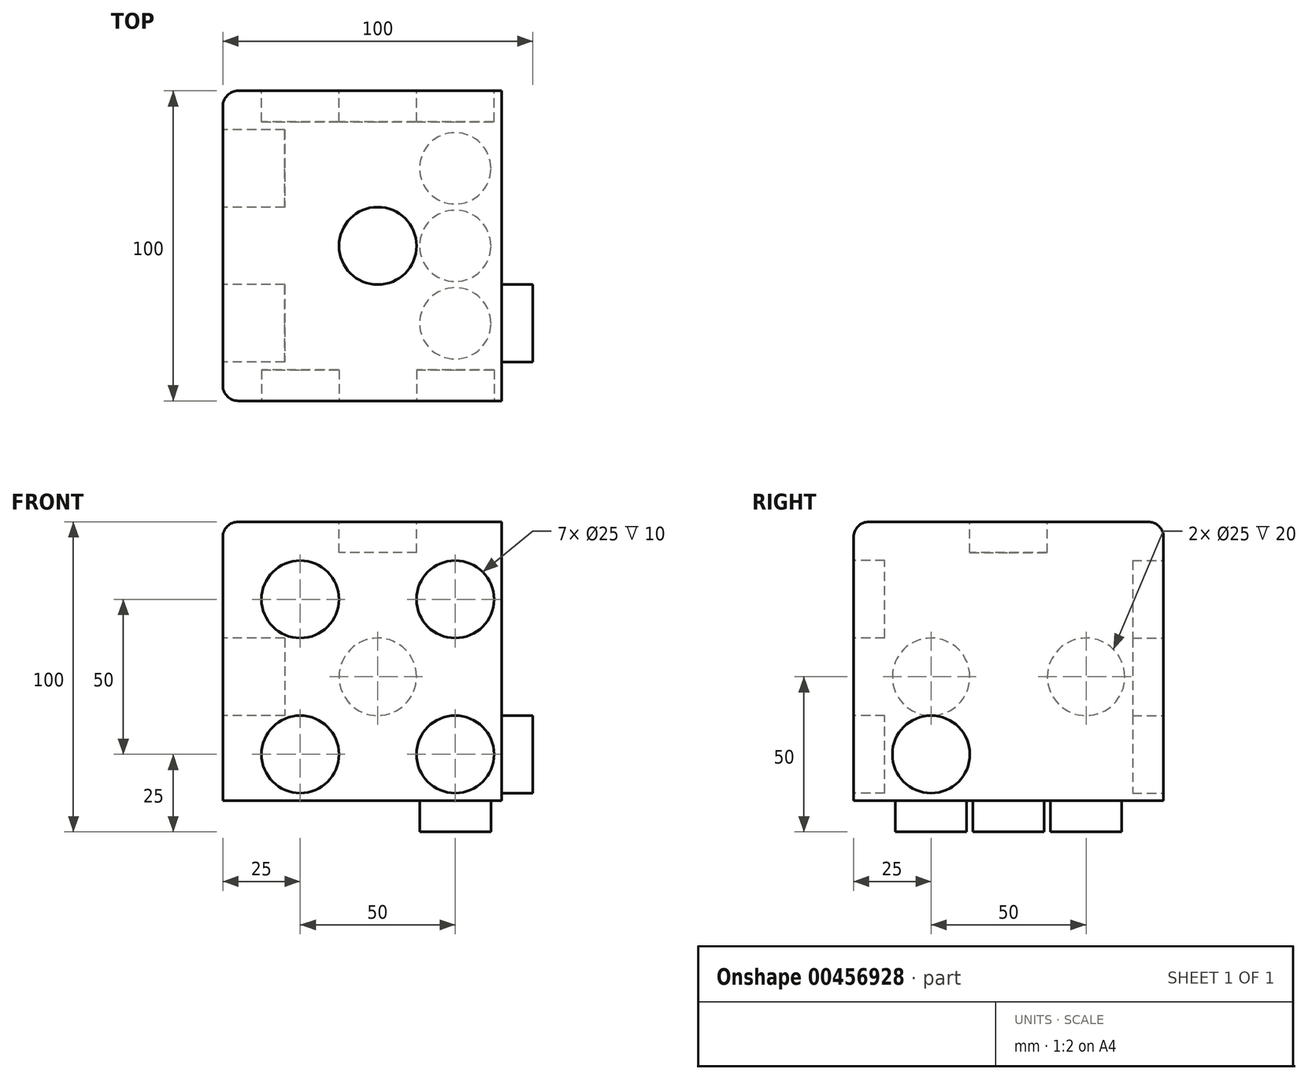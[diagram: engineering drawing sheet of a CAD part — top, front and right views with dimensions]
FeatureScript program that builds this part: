
annotation { "Feature Type Name" : "Feature", "Feature Type Description" : "" }
export const myFeature = defineFeature(function(context is Context, id is Id, definition is map)
    precondition{}
    {
        {
            var Q0;
            Q0=qCreatedBy(makeId("Top.planeOp"),FACE);
            var sketch = newSketch(context, id + "F0", { "sketchPlane" : qUnion([Q0])});
            skLineSegment(sketch, "E0.bottom", {"start": v(50, -50) * mm, "end": v(-50, -50) * mm});
            skLineSegment(sketch, "E0.top", {"start": v(50, 50) * mm, "end": v(-50, 50) * mm});
            skLineSegment(sketch, "E0.left", {"start": v(50, -50) * mm, "end": v(50, 50) * mm});
            skLineSegment(sketch, "E0.right", {"start": v(-50, -50) * mm, "end": v(-50, 50) * mm});
            skPoint(sketch, "E0.middle", {"position": v(0, 0) * mm});
            skLineSegment(sketch, "E1", {"start": v(-50, 50) * mm, "end": v(50, -50) * mm, "construction": true});
            skLineSegment(sketch, "E2", {"start": v(-50, -50) * mm, "end": v(50, 50) * mm, "construction": true});
            skLineSegment(sketch, "E3", {"start": v(-50, 0) * mm, "end": v(50, 0) * mm, "construction": true});
            skLineSegment(sketch, "E4", {"start": v(0, 50) * mm, "end": v(0, -50) * mm, "construction": true});
            skSolve(sketch);
        }
        {
            var Q0;
            Q0=makeQuery(id+"F0.imprint","IMPRINT",FACE,{"disambiguationData":[TD([[makeQuery(id+"F0.imprint","IMPRINT",EDGE,{"derivedFrom":sQuery(id+"F0.wireOp",EDGE,"E0.bottom")}),-1.0]])]});
            extrude(context, id + "F1", {"entities" : qUnion([Q0]), "depth" : 100 * mm});
        }
        {
            var Q0;
            Q0=makeQuery(id+"F1.opExtrude","CAP_FACE",FACE,{"disambiguationData":[OSD([sQuery(id+"F0.wireOp",EDGE,"E0.bottom"),sQuery(id+"F0.wireOp",EDGE,"E0.top"),sQuery(id+"F0.wireOp",EDGE,"E0.left"),sQuery(id+"F0.wireOp",EDGE,"E0.right")])],"isStart":false});
            var sketch = newSketch(context, id + "F2", { "sketchPlane" : qUnion([Q0])});
            skSolve(sketch);
        }
        {
            var Q0;
            Q0=makeQuery(id+"F2.imprint","IMPRINT",FACE,{"disambiguationData":[TD([[makeQuery(id+"F2.imprint","IMPRINT",EDGE,{"derivedFrom":makeQuery(id+"F1.opExtrude","CAP_EDGE",EDGE,{"disambiguationData":[OSD([sQuery(id+"F0.wireOp",EDGE,"E0.bottom")])],"isStart":false})}),-1.0]])]});
            var sketch = newSketch(context, id + "F3", { "sketchPlane" : qUnion([Q0])});
            skCircle(sketch, "E5", {"center": v(0, 0) * mm, "radius": 12.5 * mm});
            skSolve(sketch);
        }
        {
            var Q0;
            Q0 = qSketchRegion(id + "F3", true);
            extrude(context, id + "F4", {"entities" : qUnion([Q0]), "operationType" : NewBodyOperationType.REMOVE, "oppositeDirection" : true, "depth" : 10 * mm});
        }
        {
            var Q0;
            Q0=makeQuery(id+"F1.opExtrude","SWEPT_FACE",FACE,{"disambiguationData":[OSD([sQuery(id+"F0.wireOp",EDGE,"E0.right")])]});
            var sketch = newSketch(context, id + "F5", { "sketchPlane" : qUnion([Q0])});
            skLineSegment(sketch, "E6", {"start": v(0, 0) * mm, "end": v(0, 100) * mm, "construction": true});
            skLineSegment(sketch, "E7", {"start": v(50, 50) * mm, "end": v(-50, 50) * mm, "construction": true});
            skLineSegment(sketch, "E8", {"start": v(-50, 100) * mm, "end": v(50, 0) * mm, "construction": true});
            skLineSegment(sketch, "E9", {"start": v(50, 100) * mm, "end": v(-50, 0) * mm, "construction": true});
            skLineSegment(sketch, "E10", {"start": v(-50, 50) * mm, "end": v(0, 100) * mm, "construction": true});
            skLineSegment(sketch, "E11", {"start": v(-50, 50) * mm, "end": v(0, 0) * mm, "construction": true});
            skLineSegment(sketch, "E12", {"start": v(-25, 75) * mm, "end": v(-25, 25) * mm, "construction": true});
            skLineSegment(sketch, "E13", {"start": v(-25, 25) * mm, "end": v(25, 25) * mm, "construction": true});
            skLineSegment(sketch, "E14", {"start": v(25, 25) * mm, "end": v(25, 75) * mm, "construction": true});
            skLineSegment(sketch, "E15", {"start": v(25, 75) * mm, "end": v(-25, 75) * mm, "construction": true});
            skSolve(sketch);
        }
        {
            var Q0;
            {var subQ0=sQuery(id+"F0.wireOp",EDGE,"E0.right");Q0=makeQuery(id+"F5.imprint","IMPRINT",FACE,{"disambiguationData":[TD([[makeQuery(id+"F5.imprint","IMPRINT",EDGE,{"derivedFrom":makeQuery(id+"F1.opExtrude","CAP_EDGE",EDGE,{"disambiguationData":[OSD([subQ0])],"isStart":true})}),-1.0]])]});}
            var sketch = newSketch(context, id + "F6", { "sketchPlane" : qUnion([Q0])});
            skSolve(sketch);
        }
        {
            var Q0;
            {var subQ0=sQuery(id+"F0.wireOp",EDGE,"E0.right");Q0=makeQuery(id+"F5.imprint","IMPRINT",FACE,{"disambiguationData":[TD([[makeQuery(id+"F5.imprint","IMPRINT",EDGE,{"derivedFrom":makeQuery(id+"F1.opExtrude","CAP_EDGE",EDGE,{"disambiguationData":[OSD([subQ0])],"isStart":true})}),-1.0]])]});}
            var sketch = newSketch(context, id + "F7", { "sketchPlane" : qUnion([Q0])});
            skCircle(sketch, "E16", {"center": v(-25, 50) * mm, "radius": 12.5 * mm});
            skCircle(sketch, "E17", {"center": v(25, 50) * mm, "radius": 12.5 * mm});
            skSolve(sketch);
        }
        {
            var Q0;
            Q0 = qSketchRegion(id + "F7", true);
            extrude(context, id + "F8", {"entities" : qUnion([Q0]), "operationType" : NewBodyOperationType.REMOVE, "oppositeDirection" : true, "depth" : 20 * mm});
        }
        {
            var Q0;
            Q0=makeQuery(id+"F1.opExtrude","SWEPT_FACE",FACE,{"disambiguationData":[OSD([sQuery(id+"F0.wireOp",EDGE,"E0.top")])]});
            var sketch = newSketch(context, id + "F9", { "sketchPlane" : qUnion([Q0])});
            skLineSegment(sketch, "E18", {"start": v(50, 100) * mm, "end": v(-50, 0) * mm, "construction": true});
            skSolve(sketch);
        }
        {
            var Q0;
            {var subQ0=sQuery(id+"F0.wireOp",EDGE,"E0.top");Q0=makeQuery(id+"F9.imprint","IMPRINT",FACE,{"disambiguationData":[TD([[makeQuery(id+"F9.imprint","IMPRINT",EDGE,{"derivedFrom":makeQuery(id+"F1.opExtrude","CAP_EDGE",EDGE,{"disambiguationData":[OSD([subQ0])],"isStart":true})}),1.0]])]});}
            var sketch = newSketch(context, id + "F10", { "sketchPlane" : qUnion([Q0])});
            skCircle(sketch, "E19", {"center": v(0, 50) * mm, "radius": 12.5 * mm});
            skSolve(sketch);
        }
        {
            var Q0;
            Q0=makeQuery(id+"F10.imprint","IMPRINT",FACE,{"disambiguationData":[TD([[makeQuery(id+"F10.imprint","IMPRINT",EDGE,{"derivedFrom":sQuery(id+"F10.wireOp",EDGE,"E19")}),-1.0]])]});
            var sketch = newSketch(context, id + "F11", { "sketchPlane" : qUnion([Q0])});
            skLineSegment(sketch, "E20", {"start": v(-50, 0) * mm, "end": v(0, 50) * mm, "construction": true});
            skLineSegment(sketch, "E21", {"start": v(0, 50) * mm, "end": v(50, 100) * mm, "construction": true});
            skLineSegment(sketch, "E22", {"start": v(0, 50) * mm, "end": v(-50, 50) * mm, "construction": true});
            skLineSegment(sketch, "E23", {"start": v(-50, 50) * mm, "end": v(0, 0) * mm, "construction": true});
            skCircle(sketch, "E24", {"center": v(-25, 25) * mm, "radius": 12.5 * mm});
            skLineSegment(sketch, "E25", {"start": v(0, 50) * mm, "end": v(50, 50) * mm, "construction": true});
            skLineSegment(sketch, "E26", {"start": v(50, 50) * mm, "end": v(0, 100) * mm, "construction": true});
            skCircle(sketch, "E27", {"center": v(25, 75) * mm, "radius": 12.5 * mm});
            skSolve(sketch);
        }
        {
            var Q0;
            Q0=makeQuery(id+"F10.imprint","IMPRINT",FACE,{"disambiguationData":[TD([[makeQuery(id+"F10.imprint","IMPRINT",EDGE,{"derivedFrom":sQuery(id+"F10.wireOp",EDGE,"E19")}),1.0]])]});
            extrude(context, id + "F12", {"entities" : qUnion([Q0]), "operationType" : NewBodyOperationType.REMOVE, "oppositeDirection" : true, "depth" : 10 * mm});
        }
        {
            var Q0;
            Q0 = qSketchRegion(id + "F11", true);
            extrude(context, id + "F13", {"entities" : qUnion([Q0]), "operationType" : NewBodyOperationType.REMOVE, "oppositeDirection" : true, "depth" : 10 * mm});
        }
        {
            var Q0;
            Q0=makeQuery(id+"F1.opExtrude","SWEPT_FACE",FACE,{"disambiguationData":[OSD([sQuery(id+"F0.wireOp",EDGE,"E0.bottom")])]});
            var sketch = newSketch(context, id + "F14", { "sketchPlane" : qUnion([Q0])});
            skLineSegment(sketch, "E28", {"start": v(0, 0) * mm, "end": v(0, 100) * mm, "construction": true});
            skLineSegment(sketch, "E29", {"start": v(50, 100) * mm, "end": v(-50, 0) * mm, "construction": true});
            skLineSegment(sketch, "E30", {"start": v(-50, 100) * mm, "end": v(50, 0) * mm, "construction": true});
            skLineSegment(sketch, "E31", {"start": v(0, 50) * mm, "end": v(50, 50) * mm, "construction": true});
            skLineSegment(sketch, "E32", {"start": v(50, 50) * mm, "end": v(-50, 50) * mm, "construction": true});
            skLineSegment(sketch, "E33", {"start": v(-50, 50) * mm, "end": v(0, 100) * mm, "construction": true});
            skLineSegment(sketch, "E34", {"start": v(50, 50) * mm, "end": v(0, 100) * mm, "construction": true});
            skLineSegment(sketch, "E35", {"start": v(-50, 50) * mm, "end": v(0, 0) * mm, "construction": true});
            skLineSegment(sketch, "E36", {"start": v(50, 50) * mm, "end": v(0, 0) * mm, "construction": true});
            skCircle(sketch, "E37", {"center": v(-25, 75) * mm, "radius": 12.5 * mm});
            skPoint(sketch, "E37.centerSnap0", {"position": v(-25, 75) * mm});
            skCircle(sketch, "E38", {"center": v(25, 75) * mm, "radius": 12.5 * mm});
            skCircle(sketch, "E39", {"center": v(-25, 25) * mm, "radius": 12.5 * mm});
            skCircle(sketch, "E40", {"center": v(25, 25) * mm, "radius": 12.5 * mm});
            skSolve(sketch);
        }
        {
            var Q0;
            Q0=makeQuery(id+"F14.imprint","IMPRINT",FACE,{"disambiguationData":[TD([[makeQuery(id+"F14.imprint","IMPRINT",EDGE,{"derivedFrom":sQuery(id+"F14.wireOp",EDGE,"E37")}),1.0]])]});
            var Q1;
            Q1=makeQuery(id+"F14.imprint","IMPRINT",FACE,{"disambiguationData":[TD([[makeQuery(id+"F14.imprint","IMPRINT",EDGE,{"derivedFrom":sQuery(id+"F14.wireOp",EDGE,"E39")}),1.0]])]});
            var Q2;
            Q2=makeQuery(id+"F14.imprint","IMPRINT",FACE,{"disambiguationData":[TD([[makeQuery(id+"F14.imprint","IMPRINT",EDGE,{"derivedFrom":sQuery(id+"F14.wireOp",EDGE,"E40")}),1.0]])]});
            var Q3;
            Q3=makeQuery(id+"F14.imprint","IMPRINT",FACE,{"disambiguationData":[TD([[makeQuery(id+"F14.imprint","IMPRINT",EDGE,{"derivedFrom":sQuery(id+"F14.wireOp",EDGE,"E38")}),1.0]])]});
            extrude(context, id + "F15", {"entities" : qUnion([Q0, Q1, Q2, Q3]), "operationType" : NewBodyOperationType.REMOVE, "oppositeDirection" : true, "depth" : 10 * mm});
        }
        {
            var Q0;
            Q0=makeQuery(id+"F1.opExtrude","SWEPT_FACE",FACE,{"disambiguationData":[OSD([sQuery(id+"F0.wireOp",EDGE,"E0.left")])]});
            var sketch = newSketch(context, id + "F16", { "sketchPlane" : qUnion([Q0])});
            skSolve(sketch);
        }
        {
            var Q0;
            {var subQ0=sQuery(id+"F0.wireOp",EDGE,"E0.left");Q0=makeQuery(id+"F16.imprint","IMPRINT",FACE,{"disambiguationData":[TD([[makeQuery(id+"F16.imprint","IMPRINT",EDGE,{"derivedFrom":makeQuery(id+"F1.opExtrude","CAP_EDGE",EDGE,{"disambiguationData":[OSD([subQ0])],"isStart":true})}),1.0]])]});}
            var sketch = newSketch(context, id + "F17", { "sketchPlane" : qUnion([Q0])});
            skLineSegment(sketch, "E41", {"start": v(0, 0) * mm, "end": v(0, 100) * mm, "construction": true});
            skLineSegment(sketch, "E42", {"start": v(50, 0) * mm, "end": v(-50, 100) * mm, "construction": true});
            skLineSegment(sketch, "E43", {"start": v(50, 100) * mm, "end": v(-50, 0) * mm, "construction": true});
            skLineSegment(sketch, "E44", {"start": v(-50, 50) * mm, "end": v(50, 50) * mm, "construction": true});
            skPoint(sketch, "E44.startSnap0", {"position": v(0, 50) * mm});
            skPoint(sketch, "E44.endSnap0", {"position": v(0, 50) * mm});
            skLineSegment(sketch, "E45", {"start": v(-50, 50) * mm, "end": v(0, 100) * mm, "construction": true});
            skLineSegment(sketch, "E46", {"start": v(50, 50) * mm, "end": v(0, 100) * mm, "construction": true});
            skLineSegment(sketch, "E47", {"start": v(-50, 50) * mm, "end": v(0, 0) * mm, "construction": true});
            skLineSegment(sketch, "E48", {"start": v(0, 0) * mm, "end": v(50, 50) * mm, "construction": true});
            skCircle(sketch, "E49", {"center": v(0, 50) * mm, "radius": 12.5 * mm});
            skCircle(sketch, "E50", {"center": v(-25, 75) * mm, "radius": 12.5 * mm});
            skPoint(sketch, "E50.centerSnap0", {"position": v(-25, 75) * mm});
            skCircle(sketch, "E51", {"center": v(25, 75) * mm, "radius": 12.5 * mm});
            skPoint(sketch, "E51.centerSnap0", {"position": v(25, 75) * mm});
            skCircle(sketch, "E52", {"center": v(25, 25) * mm, "radius": 12.5 * mm});
            skCircle(sketch, "E53.MirrorC", {"center": v(-25, 25) * mm, "radius": 12.5 * mm});
            skSolve(sketch);
        }
        {
            var Q0;
            Q0=makeQuery(id+"F17.imprint","IMPRINT",FACE,{"disambiguationData":[TD([[makeQuery(id+"F17.imprint","IMPRINT",EDGE,{"derivedFrom":sQuery(id+"F17.wireOp",EDGE,"E50")}),1.0]])]});
            var Q1;
            Q1=makeQuery(id+"F17.imprint","IMPRINT",FACE,{"disambiguationData":[TD([[makeQuery(id+"F17.imprint","IMPRINT",EDGE,{"derivedFrom":sQuery(id+"F17.wireOp",EDGE,"E51")}),1.0]])]});
            var Q2;
            Q2=makeQuery(id+"F17.imprint","IMPRINT",FACE,{"disambiguationData":[TD([[makeQuery(id+"F17.imprint","IMPRINT",EDGE,{"derivedFrom":sQuery(id+"F17.wireOp",EDGE,"E53.MirrorC")}),-1.0]])]});
            var Q3;
            Q3=makeQuery(id+"F17.imprint","IMPRINT",FACE,{"disambiguationData":[TD([[makeQuery(id+"F17.imprint","IMPRINT",EDGE,{"derivedFrom":sQuery(id+"F17.wireOp",EDGE,"E52")}),1.0]])]});
            var Q4;
            Q4=makeQuery(id+"F17.imprint","IMPRINT",FACE,{"disambiguationData":[TD([[makeQuery(id+"F17.imprint","IMPRINT",EDGE,{"derivedFrom":sQuery(id+"F17.wireOp",EDGE,"E49")}),1.0]])]});
            extrude(context, id + "F18", {"entities" : qUnion([Q0, Q1, Q2, Q3, Q4]), "operationType" : NewBodyOperationType.REMOVE, "oppositeDirection" : true, "depth" : 10 * mm});
        }
        {
            var Q0;
            Q0=makeQuery(id+"F1.opExtrude","CAP_FACE",FACE,{"disambiguationData":[OSD([sQuery(id+"F0.wireOp",EDGE,"E0.bottom"),sQuery(id+"F0.wireOp",EDGE,"E0.top"),sQuery(id+"F0.wireOp",EDGE,"E0.left"),sQuery(id+"F0.wireOp",EDGE,"E0.right")])],"isStart":true});
            var sketch = newSketch(context, id + "F19", { "sketchPlane" : qUnion([Q0])});
            skLineSegment(sketch, "E54", {"start": v(0, 50) * mm, "end": v(0, -50) * mm, "construction": true});
            skLineSegment(sketch, "E55", {"start": v(-50, 0) * mm, "end": v(50, 0) * mm, "construction": true});
            skLineSegment(sketch, "E56", {"start": v(-50, 25) * mm, "end": v(50, 25) * mm, "construction": true});
            skLineSegment(sketch, "E57", {"start": v(-25, 50) * mm, "end": v(-25, -50) * mm, "construction": true});
            skLineSegment(sketch, "E58", {"start": v(25, 50) * mm, "end": v(25, -50) * mm, "construction": true});
            skLineSegment(sketch, "E59", {"start": v(-50, -25) * mm, "end": v(50, -25) * mm, "construction": true});
            skCircle(sketch, "E60", {"center": v(-25, 25) * mm, "radius": 11.5 * mm});
            skCircle(sketch, "E61", {"center": v(-25, 0) * mm, "radius": 11.5 * mm});
            skCircle(sketch, "E62", {"center": v(-25, -25) * mm, "radius": 11.5 * mm});
            skCircle(sketch, "E63.MirrorC", {"center": v(25, 25) * mm, "radius": 11.5 * mm});
            skCircle(sketch, "E64.MirrorC", {"center": v(25, 0) * mm, "radius": 11.5 * mm});
            skCircle(sketch, "E65.MirrorC", {"center": v(25, -25) * mm, "radius": 11.5 * mm});
            skSolve(sketch);
        }
        {
            var Q0;
            Q0=makeQuery(id+"F19.imprint","IMPRINT",FACE,{"disambiguationData":[TD([[makeQuery(id+"F19.imprint","IMPRINT",EDGE,{"derivedFrom":sQuery(id+"F19.wireOp",EDGE,"E60")}),1.0]])]});
            var Q1;
            Q1=makeQuery(id+"F19.imprint","IMPRINT",FACE,{"disambiguationData":[TD([[makeQuery(id+"F19.imprint","IMPRINT",EDGE,{"derivedFrom":sQuery(id+"F19.wireOp",EDGE,"E61")}),1.0]])]});
            var Q2;
            Q2=makeQuery(id+"F19.imprint","IMPRINT",FACE,{"disambiguationData":[TD([[makeQuery(id+"F19.imprint","IMPRINT",EDGE,{"derivedFrom":sQuery(id+"F19.wireOp",EDGE,"E62")}),1.0]])]});
            var Q3;
            Q3=makeQuery(id+"F19.imprint","IMPRINT",FACE,{"disambiguationData":[TD([[makeQuery(id+"F19.imprint","IMPRINT",EDGE,{"derivedFrom":sQuery(id+"F19.wireOp",EDGE,"E65.MirrorC")}),-1.0]])]});
            var Q4;
            Q4=makeQuery(id+"F19.imprint","IMPRINT",FACE,{"disambiguationData":[TD([[makeQuery(id+"F19.imprint","IMPRINT",EDGE,{"derivedFrom":sQuery(id+"F19.wireOp",EDGE,"E64.MirrorC")}),-1.0]])]});
            var Q5;
            Q5=makeQuery(id+"F19.imprint","IMPRINT",FACE,{"disambiguationData":[TD([[makeQuery(id+"F19.imprint","IMPRINT",EDGE,{"derivedFrom":sQuery(id+"F19.wireOp",EDGE,"E63.MirrorC")}),-1.0]])]});
            extrude(context, id + "F20", {"entities" : qUnion([Q0, Q1, Q2, Q3, Q4, Q5]), "operationType" : NewBodyOperationType.REMOVE, "oppositeDirection" : true, "depth" : 10 * mm});
        }
        {
            var Q0;
            Q0=makeQuery(id+"F1.opExtrude","SWEPT_EDGE",EDGE,{"disambiguationData":[OSD([sQuery(id+"F0.wireOp",EDGE,"E0.top"),sQuery(id+"F0.wireOp",EDGE,"E0.right")])]});
            var Q1;
            Q1=makeQuery(id+"F1.opExtrude","CAP_EDGE",EDGE,{"disambiguationData":[OSD([sQuery(id+"F0.wireOp",EDGE,"E0.top")])],"isStart":false});
            var Q2;
            Q2=makeQuery(id+"F1.opExtrude","SWEPT_EDGE",EDGE,{"disambiguationData":[OSD([sQuery(id+"F0.wireOp",EDGE,"E0.top"),sQuery(id+"F0.wireOp",EDGE,"E0.left")])]});
            var Q3;
            Q3=makeQuery(id+"F1.opExtrude","CAP_EDGE",EDGE,{"disambiguationData":[OSD([sQuery(id+"F0.wireOp",EDGE,"E0.top")])],"isStart":true});
            var Q4;
            Q4=makeQuery(id+"F1.opExtrude","CAP_EDGE",EDGE,{"disambiguationData":[OSD([sQuery(id+"F0.wireOp",EDGE,"E0.left")])],"isStart":true});
            var Q5;
            Q5=makeQuery(id+"F1.opExtrude","CAP_EDGE",EDGE,{"disambiguationData":[OSD([sQuery(id+"F0.wireOp",EDGE,"E0.bottom")])],"isStart":true});
            var Q6;
            Q6=makeQuery(id+"F1.opExtrude","CAP_EDGE",EDGE,{"disambiguationData":[OSD([sQuery(id+"F0.wireOp",EDGE,"E0.right")])],"isStart":true});
            var Q7;
            Q7=makeQuery(id+"F1.opExtrude","SWEPT_EDGE",EDGE,{"disambiguationData":[OSD([sQuery(id+"F0.wireOp",EDGE,"E0.bottom"),sQuery(id+"F0.wireOp",EDGE,"E0.right")])]});
            var Q8;
            Q8=makeQuery(id+"F1.opExtrude","SWEPT_EDGE",EDGE,{"disambiguationData":[OSD([sQuery(id+"F0.wireOp",EDGE,"E0.bottom"),sQuery(id+"F0.wireOp",EDGE,"E0.left")])]});
            var Q9;
            Q9=makeQuery(id+"F1.opExtrude","CAP_EDGE",EDGE,{"disambiguationData":[OSD([sQuery(id+"F0.wireOp",EDGE,"E0.left")])],"isStart":false});
            var Q10;
            Q10=makeQuery(id+"F1.opExtrude","CAP_EDGE",EDGE,{"disambiguationData":[OSD([sQuery(id+"F0.wireOp",EDGE,"E0.bottom")])],"isStart":false});
            var Q11;
            Q11=makeQuery(id+"F1.opExtrude","CAP_EDGE",EDGE,{"disambiguationData":[OSD([sQuery(id+"F0.wireOp",EDGE,"E0.right")])],"isStart":false});
            fillet(context, id + "F21", {"entities" : qUnion([Q0, Q1, Q2, Q3, Q4, Q5, Q6, Q7, Q8, Q9, Q10, Q11]), "radius" : 5 * mm, "tangentPropagation" : true, "allowEdgeOverflow" : false});
        }
    });
